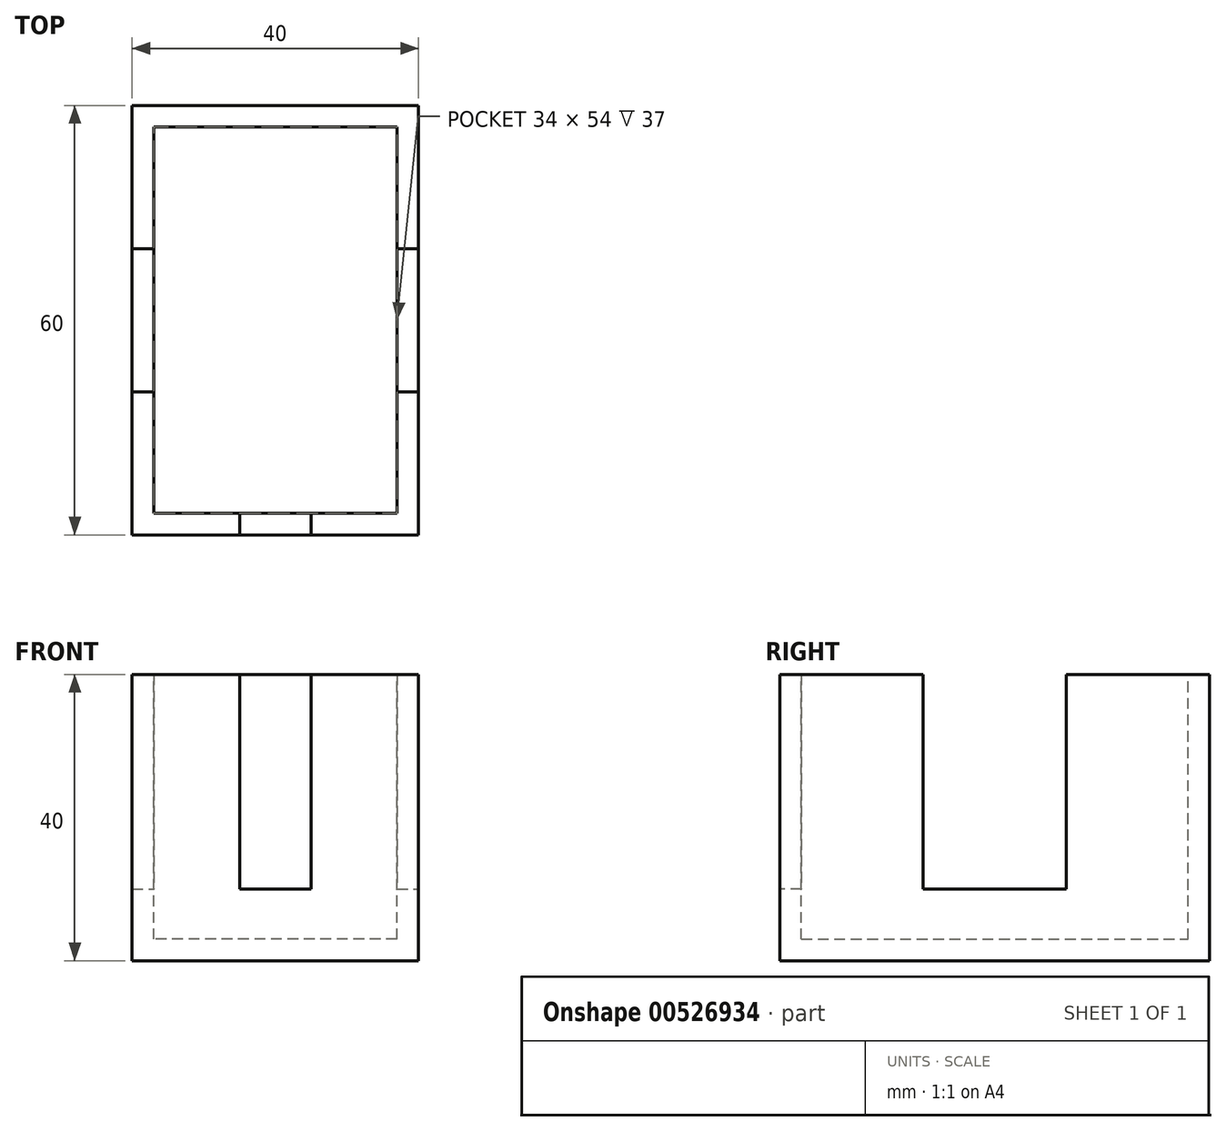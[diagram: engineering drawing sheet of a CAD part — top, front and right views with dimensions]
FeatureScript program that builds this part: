
annotation { "Feature Type Name" : "Feature", "Feature Type Description" : "" }
export const myFeature = defineFeature(function(context is Context, id is Id, definition is map)
    precondition{}
    {
        {
            var Q0;
            Q0=qCreatedBy(makeId("Front.planeOp"),FACE);
            var sketch = newSketch(context, id + "F0", { "sketchPlane" : qUnion([Q0])});
            skLineSegment(sketch, "E0.bottom", {"start": v(20, 20) * mm, "end": v(-20, 20) * mm});
            skLineSegment(sketch, "E0.top", {"start": v(20, -20) * mm, "end": v(-20, -20) * mm});
            skLineSegment(sketch, "E0.left", {"start": v(20, 20) * mm, "end": v(20, -20) * mm});
            skLineSegment(sketch, "E0.right", {"start": v(-20, 20) * mm, "end": v(-20, -20) * mm});
            skPoint(sketch, "E0.middle", {"position": v(0, 0) * mm});
            skSolve(sketch);
        }
        {
            var Q0;
            Q0 = qSketchRegion(id + "F0", true);
            extrude(context, id + "F1", {"entities" : qUnion([Q0]), "depth" : 60 * mm, "offsetDistance" : 25 * mm});
        }
        {
            var Q0;
            Q0=makeQuery(id+"F1.opExtrude","SWEPT_FACE",FACE,{"disambiguationData":[OSD([sQuery(id+"F0.wireOp",EDGE,"E0.bottom")])]});
            var sketch = newSketch(context, id + "F2", { "sketchPlane" : qUnion([Q0])});
            skPoint(sketch, "E1.end.orphan", {"position": v(0, -60) * mm});
            skPoint(sketch, "E2.end.orphan", {"position": v(0, -30) * mm});
            skPoint(sketch, "E2.start.orphan", {"position": v(0, 0) * mm});
            skLineSegment(sketch, "E3.bottom", {"start": v(17, -57) * mm, "end": v(-17, -57) * mm});
            skLineSegment(sketch, "E3.top", {"start": v(17, -3) * mm, "end": v(-17, -3) * mm});
            skLineSegment(sketch, "E3.left", {"start": v(17, -57) * mm, "end": v(17, -3) * mm});
            skLineSegment(sketch, "E3.right", {"start": v(-17, -57) * mm, "end": v(-17, -3) * mm});
            skSolve(sketch);
        }
        {
            var Q0;
            Q0 = qSketchRegion(id + "F2", true);
            extrude(context, id + "F3", {"entities" : qUnion([Q0]), "operationType" : NewBodyOperationType.REMOVE, "endBound" : BoundingType.UP_TO_NEXT, "oppositeDirection" : true, "depth" : 25 * mm, "hasOffset" : true, "offsetDistance" : 3 * mm});
        }
        {
            var Q0;
            Q0=makeQuery(id+"F1.opExtrude","SWEPT_FACE",FACE,{"disambiguationData":[OSD([sQuery(id+"F0.wireOp",EDGE,"E0.left")])]});
            var sketch = newSketch(context, id + "F4", { "sketchPlane" : qUnion([Q0])});
            skPoint(sketch, "E4.end.orphan", {"position": v(0, 0) * mm});
            skPoint(sketch, "E5.end.orphan", {"position": v(-30, 0) * mm});
            skPoint(sketch, "E5.start.orphan", {"position": v(-60, 0) * mm});
            skPoint(sketch, "E6", {"position": v(-30, 5) * mm});
            skLineSegment(sketch, "E7.bottom", {"start": v(-20, 20) * mm, "end": v(-40, 20) * mm});
            skLineSegment(sketch, "E7.top", {"start": v(-20, -10) * mm, "end": v(-40, -10) * mm});
            skLineSegment(sketch, "E7.left", {"start": v(-20, 20) * mm, "end": v(-20, -10) * mm});
            skLineSegment(sketch, "E7.right", {"start": v(-40, 20) * mm, "end": v(-40, -10) * mm});
            skSolve(sketch);
        }
        {
            var Q0;
            Q0 = qSketchRegion(id + "F4", true);
            extrude(context, id + "F5", {"entities" : qUnion([Q0]), "operationType" : NewBodyOperationType.REMOVE, "endBound" : BoundingType.THROUGH_ALL, "oppositeDirection" : true, "depth" : 25 * mm, "offsetDistance" : 25 * mm});
        }
        {
            var Q0;
            Q0=makeQuery(id+"F1.opExtrude","CAP_FACE",FACE,{"disambiguationData":[OSD([sQuery(id+"F0.wireOp",EDGE,"E0.bottom"),sQuery(id+"F0.wireOp",EDGE,"E0.top"),sQuery(id+"F0.wireOp",EDGE,"E0.left"),sQuery(id+"F0.wireOp",EDGE,"E0.right")])],"isStart":false});
            var sketch = newSketch(context, id + "F6", { "sketchPlane" : qUnion([Q0])});
            skPoint(sketch, "E8", {"position": v(0, 5) * mm});
            skLineSegment(sketch, "E9.bottom", {"start": v(5, 20) * mm, "end": v(-5, 20) * mm});
            skLineSegment(sketch, "E9.top", {"start": v(5, -10) * mm, "end": v(-5, -10) * mm});
            skLineSegment(sketch, "E9.left", {"start": v(5, 20) * mm, "end": v(5, -10) * mm});
            skLineSegment(sketch, "E9.right", {"start": v(-5, 20) * mm, "end": v(-5, -10) * mm});
            skSolve(sketch);
        }
        {
            var Q0;
            Q0 = qSketchRegion(id + "F6", true);
            extrude(context, id + "F7", {"entities" : qUnion([Q0]), "operationType" : NewBodyOperationType.REMOVE, "endBound" : BoundingType.UP_TO_NEXT, "oppositeDirection" : true, "depth" : 25 * mm, "offsetDistance" : 25 * mm});
        }
    });
